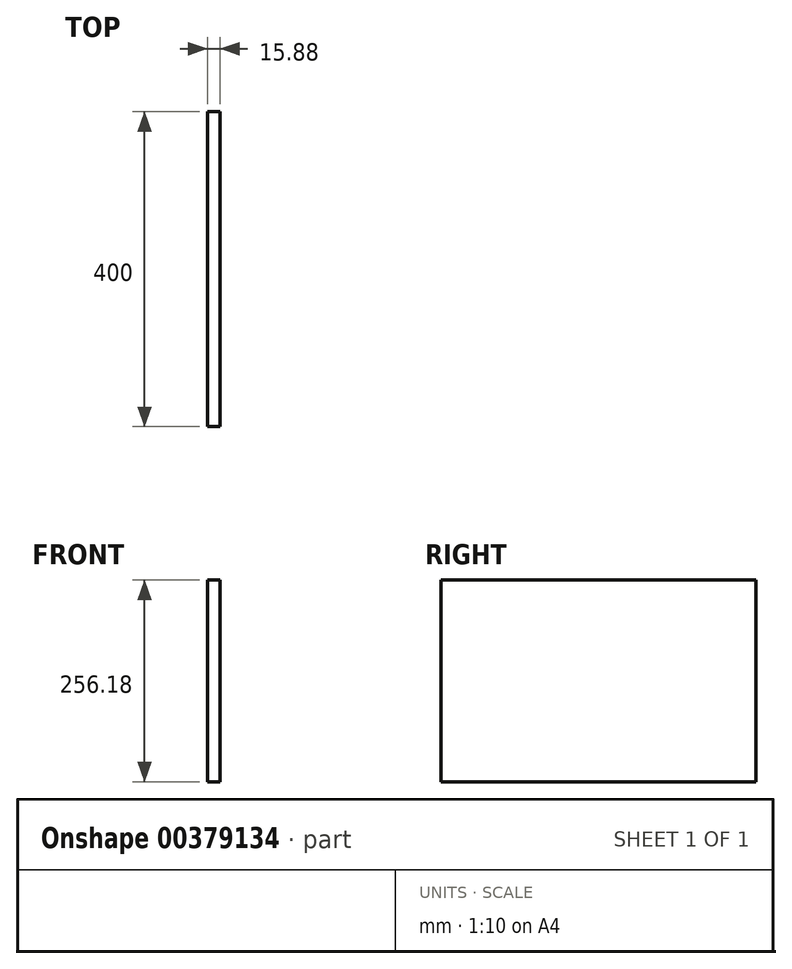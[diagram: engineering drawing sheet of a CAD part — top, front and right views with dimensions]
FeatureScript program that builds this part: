
annotation { "Feature Type Name" : "Feature", "Feature Type Description" : "" }
export const myFeature = defineFeature(function(context is Context, id is Id, definition is map)
    precondition{}
    {
        {
            var Q0;
            Q0=qCreatedBy(makeId("Front.planeOp"),FACE);
            var sketch = newSketch(context, id + "F0", { "sketchPlane" : qUnion([Q0])});
            skLineSegment(sketch, "E0.bottom", {"start": v(7.94, -128.1) * mm, "end": v(-7.94, -128.1) * mm});
            skLineSegment(sketch, "E0.top", {"start": v(7.94, 128.1) * mm, "end": v(-7.94, 128.1) * mm});
            skLineSegment(sketch, "E0.left", {"start": v(7.94, -128.1) * mm, "end": v(7.94, 128.1) * mm});
            skLineSegment(sketch, "E0.right", {"start": v(-7.94, -128.1) * mm, "end": v(-7.94, 128.1) * mm});
            skPoint(sketch, "E0.middle", {"position": v(0, 0) * mm});
            skSolve(sketch);
        }
        {
            var Q0;
            Q0=makeQuery(id+"F0.imprint","IMPRINT",FACE,{"disambiguationData":[TD([[makeQuery(id+"F0.imprint","IMPRINT",EDGE,{"derivedFrom":sQuery(id+"F0.wireOp",EDGE,"E0.bottom")}),-1.0]])]});
            extrude(context, id + "F1", {"entities" : qUnion([Q0]), "depth" : 400 * mm});
        }
    });
